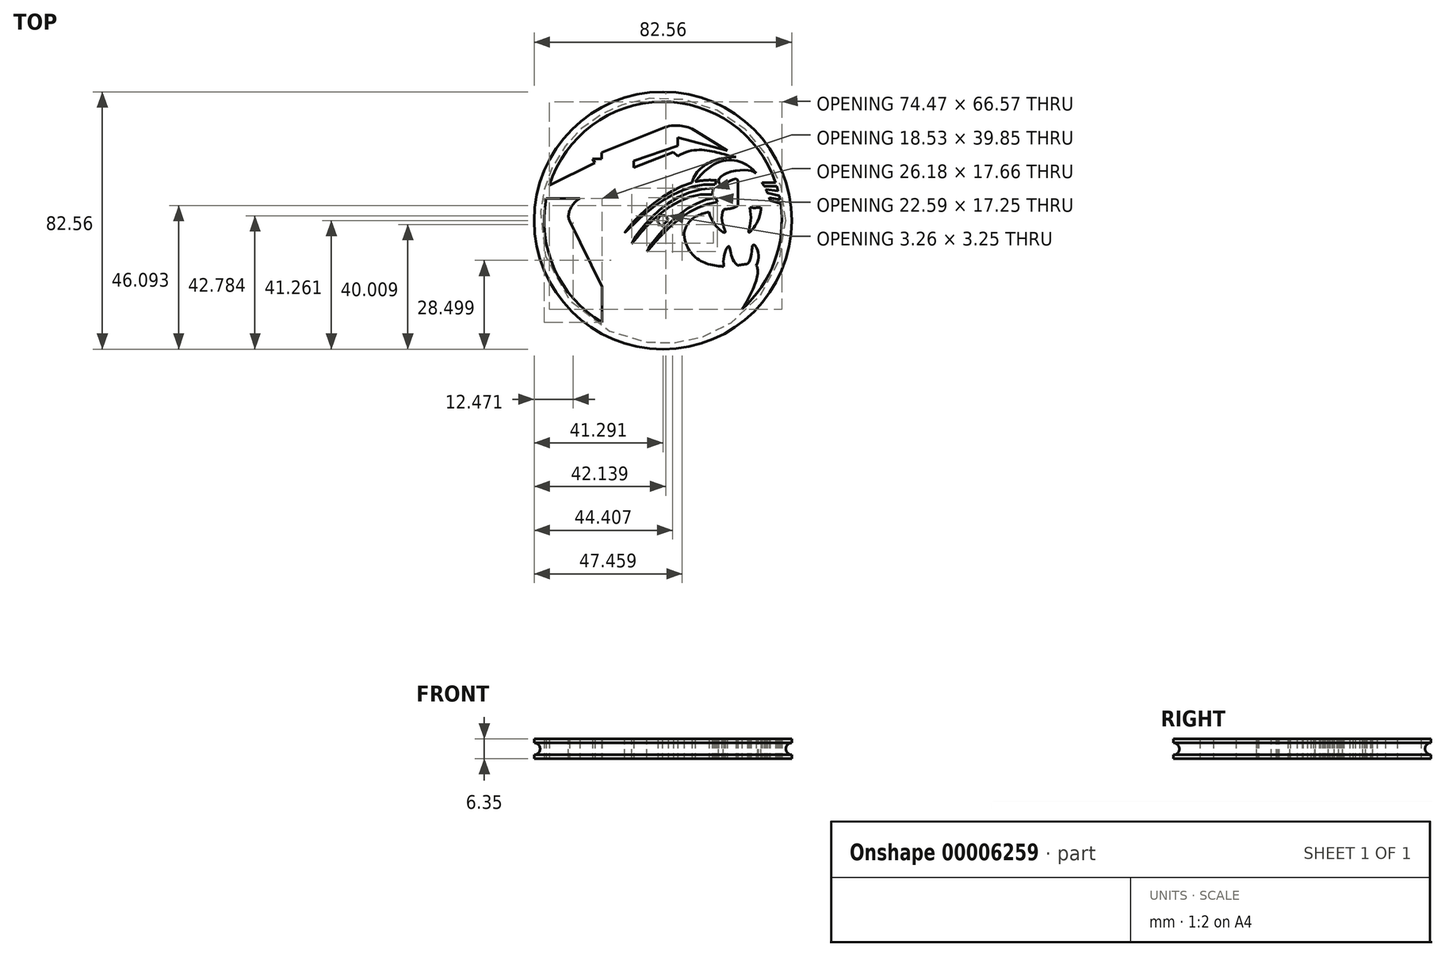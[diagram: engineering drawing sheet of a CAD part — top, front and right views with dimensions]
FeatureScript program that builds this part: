
annotation { "Feature Type Name" : "Feature", "Feature Type Description" : "" }
export const myFeature = defineFeature(function(context is Context, id is Id, definition is map)
    precondition{}
    {
        {
            var Q0;
            Q0=qCreatedBy(makeId("Top.planeOp"),FACE);
            var sketch = newSketch(context, id + "F0", { "sketchPlane" : qUnion([Q0])});
            skCircle(sketch, "E0", {"center": v(0, 0) * mm, "radius": 41.28 * mm});
            skArc(sketch, "E1", {"start": v(1.64, 0.23) * mm, "mid": v(-1.19, 1.15) * mm, "end": v(-0.18, -1.65) * mm});
            skLineSegment(sketch, "E2", {"start": v(-19.54, -32.7) * mm, "end": v(-19.54, -21.25) * mm});
            skLineSegment(sketch, "E3", {"start": v(-19.54, -21.25) * mm, "end": v(-29.91, 0) * mm});
            skLineSegment(sketch, "E4", {"start": v(-26.6, 7.14) * mm, "end": v(-37.42, 7.14) * mm});
            skLineSegment(sketch, "E5", {"start": v(-18.79, -32.25) * mm, "end": v(-5.5, -24.25) * mm});
            skLineSegment(sketch, "E6", {"start": v(-5.5, -24.25) * mm, "end": v(-5.4, -31.69) * mm});
            skLineSegment(sketch, "E7", {"start": v(-5.4, -31.69) * mm, "end": v(8.85, -23.41) * mm});
            skLineSegment(sketch, "E8", {"start": v(8.85, -23.41) * mm, "end": v(8.96, -29.7) * mm});
            skFitSpline(sketch, "E9", {"points": [v(-29.91, 0) * mm, v(-23.1, 7.14) * mm], "startDerivative": vector(-5.28, 8.66) * mm, "endDerivative": vector(10.77, -7.17) * mm});
            skFitSpline(sketch, "E10", {"points": [v(8.96, -29.7) * mm, v(25.32, -28.47) * mm, v(25.32, -28.47) * mm], "startDerivative": vector(47.44, 39.7) * mm, "endDerivative": vector(-1.95, -1.88) * mm});
            skFitSpline(sketch, "E11", {"points": [v(5.73, 0) * mm, v(22.6, -14.56) * mm, v(29.9, -14.48) * mm, v(25.32, -28.47) * mm], "startDerivative": vector(21.9, -103.44) * mm, "endDerivative": vector(-35.34, -54.97) * mm});
            skFitSpline(sketch, "E12", {"points": [v(19.52, -14.73) * mm, v(21.08, -8.23) * mm, v(23.84, -14.4) * mm], "startDerivative": vector(-3.49, 18.5) * mm, "endDerivative": vector(14.85, -13.43) * mm});
            skFitSpline(sketch, "E13", {"points": [v(27.14, -13.91) * mm, v(28.93, -7.84) * mm, v(29.9, -14.48) * mm], "startDerivative": vector(10.02, 12.43) * mm, "endDerivative": vector(-10.7, -20.61) * mm});
            skFitSpline(sketch, "E14", {"points": [v(17.17, 12.86) * mm, v(-12.25, -3.88) * mm, v(16.61, 11.6) * mm], "startDerivative": vector(-89.6, 11.15) * mm, "endDerivative": vector(89, -6.61) * mm});
            skFitSpline(sketch, "E15", {"points": [v(16.9, 7.36) * mm, v(-5.11, -9.9) * mm, v(17.47, 5.88) * mm], "startDerivative": vector(-73.1, -8.45) * mm, "endDerivative": vector(72.62, 6.22) * mm});
            skFitSpline(sketch, "E16", {"points": [v(16.21, 10.34) * mm, v(-9.95, -7.33) * mm, v(15.8, 8.37) * mm], "startDerivative": vector(-96.18, 0.86) * mm, "endDerivative": vector(86.53, -8.08) * mm});
            skLineSegment(sketch, "E17", {"start": v(17.17, 12.86) * mm, "end": v(16.61, 11.6) * mm});
            skLineSegment(sketch, "E18", {"start": v(15.8, 8.37) * mm, "end": v(16.21, 10.34) * mm});
            skLineSegment(sketch, "E19", {"start": v(25.17, -28.06) * mm, "end": v(25.17, -28.6) * mm});
            skArc(sketch, "E20.trimOffspring", {"start": v(25.32, -28.47) * mm, "mid": v(25.32, -28.47) * mm, "end": v(25.32, -28.47) * mm});
            skFitSpline(sketch, "E21", {"points": [v(19.52, -14.73) * mm, v(6.73, -4.5) * mm], "startDerivative": vector(-16.71, 0.55) * mm, "endDerivative": vector(-2.84, 23.57) * mm});
            skFitSpline(sketch, "E22", {"points": [v(6.73, -4.5) * mm, v(24.02, 5.49) * mm], "startDerivative": vector(3.4, 31.15) * mm, "endDerivative": vector(-2.16, 10.6) * mm});
            skLineSegment(sketch, "E23", {"start": v(16.9, 7.36) * mm, "end": v(17.47, 5.88) * mm});
            skFitSpline(sketch, "E24", {"points": [v(14.73, 2.8) * mm, v(19.94, -3.75) * mm, v(19.45, 3.55) * mm], "startDerivative": vector(6.41, -26.93) * mm, "endDerivative": vector(10.42, 21.37) * mm});
            skFitSpline(sketch, "E25", {"points": [v(27.67, 4.58) * mm, v(27.6, -3.8) * mm, v(31.36, 4.4) * mm], "startDerivative": vector(8.56, -28.07) * mm, "endDerivative": vector(-2.05, 22.89) * mm});
            skLineSegment(sketch, "E26", {"start": v(24.02, 5.49) * mm, "end": v(24.02, 11.88) * mm});
            skLineSegment(sketch, "E27", {"start": v(25.3, 4.42) * mm, "end": v(25.3, 11.7) * mm});
            skFitSpline(sketch, "E28", {"points": [v(25.3, 4.42) * mm, v(34.47, 6.01) * mm, v(31.22, 13.97) * mm], "startDerivative": vector(35.54, -5.04) * mm, "endDerivative": vector(-23.07, 27.5) * mm});
            skFitSpline(sketch, "E29", {"points": [v(24.02, 11.88) * mm, v(23.68, 13.31) * mm, v(21.16, 12.54) * mm, v(18.79, 11.5) * mm, v(17.83, 12.73) * mm, v(20.32, 15.16) * mm, v(27.31, 16.14) * mm, v(30.32, 14.85) * mm, v(31.22, 13.3) * mm, v(28.65, 13.48) * mm, v(27.36, 13.61) * mm, v(26.07, 13.6) * mm, v(25.3, 11.7) * mm], "startDerivative": vector(0.46, 29.16) * mm, "endDerivative": vector(-6.46, -31.38) * mm});
            skFitSpline(sketch, "E30", {"points": [v(31.35, 3.56) * mm, v(34.49, 4.23) * mm, v(30.92, 13.18) * mm, v(30.8, 13.18) * mm], "startDerivative": vector(9.9, -8.27) * mm, "endDerivative": vector(0.2, -0.12) * mm});
            skLineSegment(sketch, "E31", {"start": v(31.74, 12.2) * mm, "end": v(36.1, 12.2) * mm});
            skLineSegment(sketch, "E32", {"start": v(32.43, 11.03) * mm, "end": v(36.47, 11.03) * mm});
            skLineSegment(sketch, "E33", {"start": v(32.94, 10.04) * mm, "end": v(36.9, 9.48) * mm});
            skLineSegment(sketch, "E34", {"start": v(36.9, 9.48) * mm, "end": v(36.7, 9.72) * mm});
            skLineSegment(sketch, "E35", {"start": v(33.49, 8.85) * mm, "end": v(37.25, 8.02) * mm});
            skLineSegment(sketch, "E36", {"start": v(34.05, 7.37) * mm, "end": v(37.5, 6.69) * mm});
            skLineSegment(sketch, "E37", {"start": v(34.32, 6.45) * mm, "end": v(37.71, 5.42) * mm});
            skCircle(sketch, "E38", {"center": v(0, 0) * mm, "radius": 38.1 * mm});
            skFitSpline(sketch, "E39", {"points": [v(23.92, 20.34) * mm, v(9.34, 12.18) * mm], "startDerivative": vector(-17.59, 0.84) * mm, "endDerivative": vector(-4.58, -18.21) * mm});
            skFitSpline(sketch, "E40", {"points": [v(10.31, 12.43) * mm, v(29.92, 15.19) * mm], "startDerivative": vector(23.24, 30.99) * mm, "endDerivative": vector(11.7, -13.67) * mm});
            skLineSegment(sketch, "E41", {"start": v(23.92, 20.34) * mm, "end": v(10.6, 28.71) * mm});
            skLineSegment(sketch, "E42", {"start": v(20.6, 22.43) * mm, "end": v(4.78, 26.62) * mm});
            skLineSegment(sketch, "E43", {"start": v(4.78, 26.62) * mm, "end": v(4.78, 23.96) * mm});
            skLineSegment(sketch, "E44", {"start": v(4.78, 23.96) * mm, "end": v(-9.3, 19.16) * mm});
            skLineSegment(sketch, "E45", {"start": v(-9.3, 19.16) * mm, "end": v(-9.3, 16.97) * mm});
            skLineSegment(sketch, "E46", {"start": v(-9.3, 16.97) * mm, "end": v(3.35, 21.92) * mm});
            skLineSegment(sketch, "E47", {"start": v(3.35, 21.92) * mm, "end": v(4.69, 20.69) * mm});
            skFitSpline(sketch, "E48", {"points": [v(4.69, 20.69) * mm, v(23.38, 20.36) * mm], "startDerivative": vector(20.58, 12.42) * mm, "endDerivative": vector(16.84, -3) * mm});
            skLineSegment(sketch, "E49", {"start": v(-36.37, 11.34) * mm, "end": v(-21.83, 18.45) * mm});
            skLineSegment(sketch, "E50", {"start": v(-21.83, 18.45) * mm, "end": v(-22.5, 19.84) * mm});
            skLineSegment(sketch, "E51", {"start": v(-22.5, 19.84) * mm, "end": v(-19.66, 19.84) * mm});
            skLineSegment(sketch, "E52", {"start": v(-19.66, 19.84) * mm, "end": v(-19.66, 21.85) * mm});
            skLineSegment(sketch, "E53", {"start": v(-19.66, 21.85) * mm, "end": v(0, 29.68) * mm});
            skPoint(sketch, "E54.visualSharp", {"position": v(5.54, 31.88) * mm});
            skArc(sketch, "E54.filletArc", {"start": v(10.6, 28.71) * mm, "mid": v(5.41, 30.46) * mm, "end": v(0, 29.68) * mm});
            skLineSegment(sketch, "E55", {"start": v(-18.79, -32.25) * mm, "end": v(-19.15, -32.93) * mm});
            skLineSegment(sketch, "E56", {"start": v(25.53, -28.14) * mm, "end": v(25.64, -28.18) * mm});
            skLineSegment(sketch, "E57", {"start": v(-0.18, -1.65) * mm, "end": v(1.64, 0.23) * mm});
            skSolve(sketch);
        }
        {
            var Q0;
            Q0 = qSketchRegion(id + "F0", true);
            var Q1;
            {var subQ0=sQuery(id+"F0.wireOp",EDGE,"E12");Q1=makeQuery(id+"F0.imprint","IMPRINT",FACE,{"disambiguationData":[TD([[makeQuery(id+"F0.imprint","IMPRINT",EDGE,{"derivedFrom":subQ0}),-1.0]])]});}
            var Q2;
            {var subQ0=sQuery(id+"F0.wireOp",EDGE,"E13");Q2=makeQuery(id+"F0.imprint","IMPRINT",FACE,{"disambiguationData":[TD([[makeQuery(id+"F0.imprint","IMPRINT",EDGE,{"derivedFrom":subQ0}),-1.0]])]});}
            var Q3;
            {var subQ0=sQuery(id+"F0.wireOp",EDGE,"9d78af66-d1aa-41fc-a9f2-600b2c9dbe75");Q3=makeQuery(id+"F0.imprint","IMPRINT",FACE,{"disambiguationData":[TD([[makeQuery(id+"F0.imprint","IMPRINT",EDGE,{"derivedFrom":subQ0}),1.0]])]});}
            var Q4;
            {var subQ1=sQuery(id+"F0.wireOp",EDGE,"91f76ec8-b100-4449-a675-d3caf3ae3a79");Q4=makeQuery(id+"F0.imprint","IMPRINT",FACE,{"disambiguationData":[TD([[makeQuery(id+"F0.imprint","IMPRINT",EDGE,{"derivedFrom":subQ1}),1.0]])]});}
            var Q5;
            {var subQ0=sQuery(id+"F0.wireOp",EDGE,"c7dc1507-02c0-4cf5-9992-08b9f5c6a8ae");Q5=makeQuery(id+"F0.imprint","IMPRINT",FACE,{"disambiguationData":[TD([[makeQuery(id+"F0.imprint","IMPRINT",EDGE,{"derivedFrom":subQ0}),-1.0]])]});}
            var Q6;
            {var subQ0=sQuery(id+"F0.wireOp",EDGE,"E24");Q6=makeQuery(id+"F0.imprint","IMPRINT",FACE,{"disambiguationData":[TD([[makeQuery(id+"F0.imprint","IMPRINT",EDGE,{"derivedFrom":subQ0}),1.0]])]});}
            var Q7;
            {var subQ8=sQuery(id+"F0.wireOp",EDGE,"E25");Q7=makeQuery(id+"F0.imprint","IMPRINT",FACE,{"disambiguationData":[TD([[makeQuery(id+"F0.imprint","IMPRINT",EDGE,{"derivedFrom":subQ8}),1.0]])]});}
            var Q8;
            {var subQ0=sQuery(id+"F0.wireOp",EDGE,"E36");Q8=makeQuery(id+"F0.imprint","IMPRINT",FACE,{"disambiguationData":[TD([[makeQuery(id+"F0.imprint","IMPRINT",EDGE,{"derivedFrom":subQ0}),-1.0]])]});}
            var Q9;
            {var subQ1=sQuery(id+"F0.wireOp",EDGE,"E33");Q9=makeQuery(id+"F0.imprint","IMPRINT",FACE,{"disambiguationData":[TD([[makeQuery(id+"F0.imprint","IMPRINT",EDGE,{"derivedFrom":subQ1}),-1.0]])]});}
            var Q10;
            {var subQ1=sQuery(id+"F0.wireOp",EDGE,"E31");Q10=makeQuery(id+"F0.imprint","IMPRINT",FACE,{"disambiguationData":[TD([[makeQuery(id+"F0.imprint","IMPRINT",EDGE,{"derivedFrom":subQ1}),-1.0]])]});}
            var Q11;
            {var subQ21=sQuery(id+"F0.wireOp",EDGE,"E2");Q11=makeQuery(id+"F0.imprint","IMPRINT",FACE,{"disambiguationData":[TD([[makeQuery(id+"F0.imprint","IMPRINT",EDGE,{"derivedFrom":subQ21}),-1.0]])]});}
            var Q12;
            {var subQ0=sQuery(id+"F0.wireOp",EDGE,"E57");Q12=makeQuery(id+"F0.imprint","IMPRINT",FACE,{"disambiguationData":[TD([[makeQuery(id+"F0.imprint","IMPRINT",EDGE,{"derivedFrom":subQ0}),-1.0]])]});}
            extrude(context, id + "F1", {"entities" : qUnion([Q0, Q1, Q2, Q3, Q4, Q5, Q6, Q7, Q8, Q9, Q10, Q11, Q12]), "depth" : 6.35 * mm});
        }
        {
            var Q0;
            Q0=qCreatedBy(makeId("Right.planeOp"),FACE);
            var sketch = newSketch(context, id + "F2", { "sketchPlane" : qUnion([Q0])});
            skLineSegment(sketch, "E58", {"start": v(0, 0) * mm, "end": v(0, 8.3) * mm});
            skCircle(sketch, "E59", {"center": v(41.28, 3.18) * mm, "radius": 1.9 * mm});
            skSolve(sketch);
        }
        {
            var Q0;
            Q0=makeQuery(id+"F2.imprint","IMPRINT",FACE,{"disambiguationData":[TD([[makeQuery(id+"F2.imprint","IMPRINT",EDGE,{"derivedFrom":sQuery(id+"F2.wireOp",EDGE,"E59")}),1.0]])]});
            var Q1;
            Q1=sQuery(id+"F2.wireOp",EDGE,"E58");
            revolve(context, id + "F3", {"operationType" : NewBodyOperationType.REMOVE, "entities" : qUnion([Q0]), "axis" : qUnion([Q1]), "revolveType" : RevolveType.FULL, "oppositeDirection" : true});
        }
    });
